# Revit family: BasinMixer_ForBowls_High_Vitra_MinimaxSSeries_A41990
name_source: partatom
category: Plumbing Fixtures
revit_build: Autodesk Revit 2017 (Build: 20160225_1515(x64)
units: mm (PartAtom-declared; Revit-internal decimal feet)

## family parameters
Cut with Voids When Loaded = No
Host = Face
OmniClass Number = 23.45.55.17
OmniClass Title = Mixing Faucets
Part Type = Normal
Room Calculation Point = No
Round Connector Dimension = Use Diameter
Shared = Yes

## types (12) — shared parameters
BIMobject category = Taps & Mixers
CW Connection = Yes
Coating Material = Chrome
Color = Chrome
Default Elevation = 850 mm  [stored 2.78871 ft]
Description = Vitra Minimax S Tall Basin Mixer For Bowls
Design country = Turkey
Flow Rate(L/min. - 3 bar) = max. 9 L/min.
HW Connection = Yes
Hot Water Supply (max.) = 80 °C
Hot Water temperature, factory set to = 38 °C
IFC Classification = Sanitary Terminal
Installation instructions = https://cdn.vitra.com.tr
Main Material = Brass
Manufacturer = Vitra
Manufacturer name = Vitra
Masterformat 2014 Code = 22 40 00
Masterformat 2014 Description = Plumbing Fixtures
Min. flow pressure of = 0.5 bar
Mounting type = Countertop
NBS Referans Code = 45-35-70/371
NBS Referans Description = Water supply fittings for wash basins and troughs
Nominal Depth (mm) = 160 mm  [stored 0.524934 ft]
Nominal Height (mm) = 340 mm  [stored 1.11549 ft]
Nominal Width (mm) = 50 mm  [stored 0.164042 ft]
Number Of Connections = 2
OmniClass Code = 23.45.55.17
OmniClass Description = Mixing Faucets
Product Properties = Water Saving, Blue Life , EPD
Product Type = Tall Basin Mixer
Product certification = https://www.vitraglobal.com
Product family = Minimax S
Product group = Minimax S Tall Basin Mixer For Bowls
Range of Hot Water Supply = 5 - 65 °C
Range of flow pressure = 1 - 5 bar
Test Pressure = 16 bar
URL = https://vitraglobal.com
Uniclass 1.4 Code = L725111
Uniclass 1.4 Description = Mixer taps
Uniclass 2.0 Code = Pr_40_30_96_98
Uniclass 2.0 Description = Washbasin Tap
Uniclass 2015 Code = Pr_40_20_87_98
Uniclass 2015 Name = Washbasin Tap
Uniformat II Code = 22 40 00
Uniformat II Description = Plumbing Fixture
Vent Connection = No
Waste Connection = No
Weight Net (kg) = 1.8
Youtube = https://www.youtube.com

## per-type parameters (varying)
| type | Article No. (default) | Brand | Connection Diameter (mm) | Model | Product SKU | Product data url | Technical description | Warranty Period (Year) |
| BasinMixer-ForBowls-Vitra-MinimaxS Series-A41990ENGX | A41990ENGX | Vitra | 10 mm  [stored 0.0328084 ft] | A41990ENGX | A41990ENGX | https://www.vitra.com.tr | https://www.vitra.com.tr | 7 Years |
| BasinMixer-ForBowls-Vitra-MinimaxS Series-A41990WSA | A41990WSA | Vitra | 10 mm  [stored 0.0328084 ft] | A41990WSA | A41990WSA | https://www.vitra.com.tr | https://www.vitra.com.tr | 7 Years |
| BasinMixer-ForBowls-Vitra-MinimaxS Series-A41990VUK | A41990VUK | Vitra | 15 mm  [stored 0.0492126 ft] | A41990VUK | A41990VUK | https://www.vitra.co.uk | https://www.vitra.co.uk | 7 Years |
| BasinMixer-ForBowls-Vitra-MinimaxS Series-A41990TPX | A41990TPX | Vitra | 10 mm  [stored 0.0328084 ft] | A41990TPX | A41990TPX | https://www.vitra.com.tr | https://www.vitra.com.tr | 7 Years |
| BasinMixer-ForBowls-Vitra-MinimaxS Series-A41990STA | A41990STA | Vitra | 10 mm  [stored 0.0328084 ft] | A41990STA | A41990STA | https://www.vitra.com.tr | https://www.vitra.com.tr | 7 Years |
| BasinMixer-ForBowls-Vitra-MinimaxS Series-A41990INV | A41990INV | Vitra | 15 mm  [stored 0.0492126 ft] | A41990INV | A41990INV | https://www.vitra.com.tr | https://www.vitra.com.tr | 7 Years |
| BasinMixer-ForBowls-Vitra-MinimaxS Series-A41990EXP | A41990EXP | Vitra | 10 mm  [stored 0.0328084 ft] | A41990EXP | A41990EXP | https://www.vitra.com.tr | https://www.vitra.com.tr | 7 Years |
| BasinMixer-ForBowls-Vitra-MinimaxS Series-A41990ENR | A41990ENR | Vitra | 10 mm  [stored 0.0328084 ft] | A41990ENR | A41990ENR | https://www.vitra.com.tr | https://www.vitra.com.tr | 7 Years |
| BasinMixer-ForBowls-Vitra-MinimaxS Series-A41990ENG | A41990ENG | Vitra | 10 mm  [stored 0.0328084 ft] | A41990ENG | A41990ENG | https://www.vitra.com.tr | https://www.vitra.com.tr | 7 Years |
| BasinMixer-ForBowls-Vitra-MinimaxS Series-A41990EKM | A41990EKM | Vitra | 10 mm  [stored 0.0328084 ft] | A41990EKM | A41990EKM | https://www.vitra.com.tr | https://www.vitra.com.tr | 7 Years |
| BasinMixer-ForBowls-Vitra-MinimaxS Series-A41990EKF | A41990EKF | Vitra | 10 mm  [stored 0.0328084 ft] | A41990EKF | A41990EKF | https://www.vitra-bad.fr | https://cdn.vitra.com.tr | 7 Years |
| BasinMixer-ForBowls-Vitra-MinimaxS Series-A41990 | A41990 | Artema | 10 mm  [stored 0.0328084 ft] | A41990 | A41990 | https://www.vitra.com.tr | https://www.vitra.com.tr | 10 Years |

note: [stored X ft] marks values corroborated as IEEE doubles in the binary element streams (Revit-internal decimal feet)

## geometry (parser evidence)
native form markers: Sweep x2
no freeform markers — native parametric forms only
